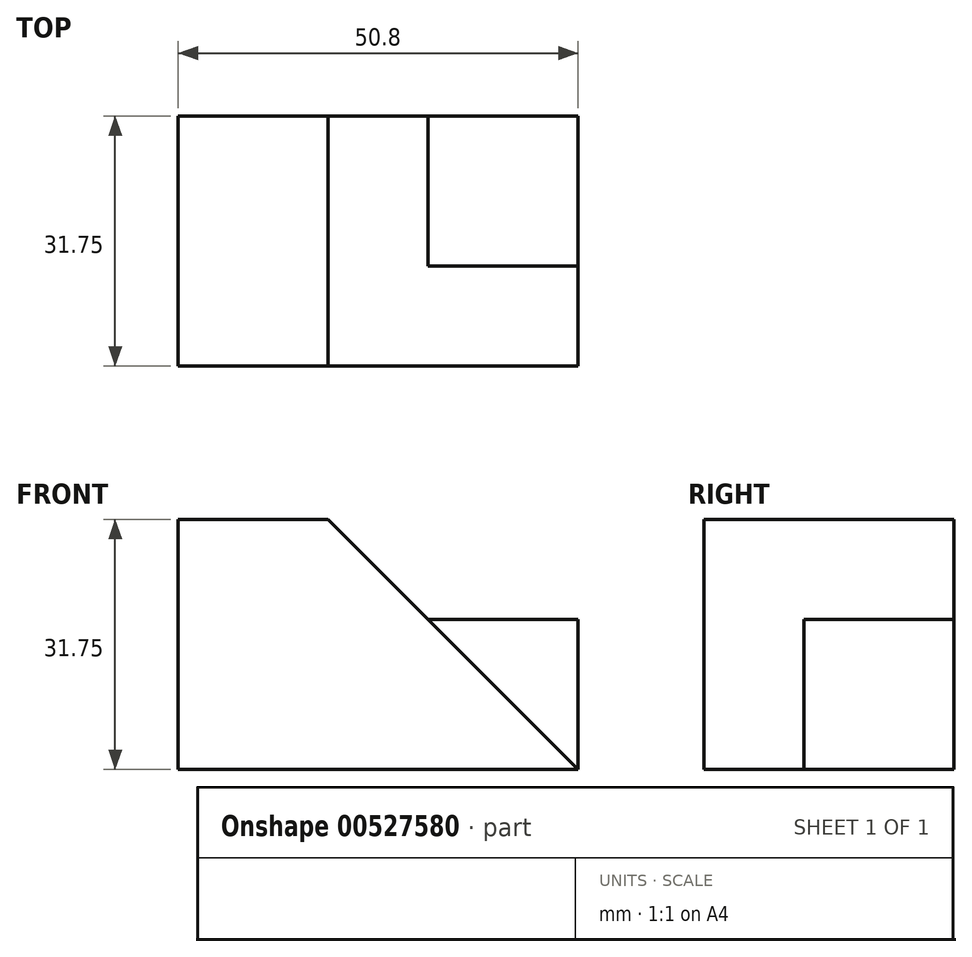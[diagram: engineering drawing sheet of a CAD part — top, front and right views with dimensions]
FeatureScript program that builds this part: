
annotation { "Feature Type Name" : "Feature", "Feature Type Description" : "" }
export const myFeature = defineFeature(function(context is Context, id is Id, definition is map)
    precondition{}
    {
        {
            var Q0;
            Q0=qCreatedBy(makeId("Front.planeOp"),FACE);
            var sketch = newSketch(context, id + "F0", { "sketchPlane" : qUnion([Q0])});
            skLineSegment(sketch, "E0", {"start": v(0, 0) * mm, "end": v(50.8, 0) * mm});
            skLineSegment(sketch, "E1", {"start": v(50.8, 0) * mm, "end": v(50.8, 31.75) * mm});
            skLineSegment(sketch, "E2", {"start": v(50.8, 31.75) * mm, "end": v(0, 31.75) * mm});
            skLineSegment(sketch, "E3", {"start": v(0, 31.75) * mm, "end": v(0, 0) * mm});
            skSolve(sketch);
        }
        {
            var Q0;
            Q0=makeQuery(id+"F0.imprint","IMPRINT",FACE,{"disambiguationData":[TD([[makeQuery(id+"F0.imprint","IMPRINT",EDGE,{"derivedFrom":sQuery(id+"F0.wireOp",EDGE,"E0")}),1.0]])]});
            extrude(context, id + "F1", {"entities" : qUnion([Q0]), "depth" : 31.75 * mm, "offsetDistance" : 25.4 * mm});
        }
        {
            var Q0;
            Q0=makeQuery(id+"F1.opExtrude","CAP_FACE",FACE,{"disambiguationData":[OSD([sQuery(id+"F0.wireOp",EDGE,"E0"),sQuery(id+"F0.wireOp",EDGE,"E1"),sQuery(id+"F0.wireOp",EDGE,"E2"),sQuery(id+"F0.wireOp",EDGE,"E3")])],"isStart":false});
            var sketch = newSketch(context, id + "F2", { "sketchPlane" : qUnion([Q0])});
            skLineSegment(sketch, "E4", {"start": v(0, 31.75) * mm, "end": v(19.05, 31.75) * mm});
            skLineSegment(sketch, "E5", {"start": v(19.05, 31.75) * mm, "end": v(50.8, 0) * mm});
            skSolve(sketch);
        }
        {
            var Q0;
            {var subQ0=sQuery(id+"F2.wireOp",EDGE,"E5");Q0=makeQuery(id+"F2.imprint","IMPRINT",FACE,{"disambiguationData":[TD([[makeQuery(id+"F2.imprint","IMPRINT",EDGE,{"derivedFrom":subQ0}),1.0]])]});}
            extrude(context, id + "F3", {"entities" : qUnion([Q0]), "operationType" : NewBodyOperationType.REMOVE, "oppositeDirection" : true, "depth" : 31.75 * mm, "offsetDistance" : 25.4 * mm});
        }
        {
            var Q0;
            Q0=makeQuery(id+"F1.opExtrude","CAP_FACE",FACE,{"disambiguationData":[OSD([sQuery(id+"F0.wireOp",EDGE,"E0"),sQuery(id+"F0.wireOp",EDGE,"E1"),sQuery(id+"F0.wireOp",EDGE,"E2"),sQuery(id+"F0.wireOp",EDGE,"E3")])],"isStart":true});
            var sketch = newSketch(context, id + "F4", { "sketchPlane" : qUnion([Q0])});
            skLineSegment(sketch, "E6", {"start": v(-50.8, 0) * mm, "end": v(-50.8, 19.05) * mm});
            skLineSegment(sketch, "E7", {"start": v(-50.8, 19.05) * mm, "end": v(-31.75, 19.05) * mm});
            skSolve(sketch);
        }
        {
            var Q0;
            {var subQ0=sQuery(id+"F4.wireOp",EDGE,"E6");Q0=makeQuery(id+"F4.imprint","IMPRINT",FACE,{"disambiguationData":[TD([[makeQuery(id+"F4.imprint","IMPRINT",EDGE,{"derivedFrom":subQ0}),-1.0]])]});}
            extrude(context, id + "F5", {"entities" : qUnion([Q0]), "oppositeDirection" : true, "depth" : 19.05 * mm, "offsetDistance" : 25.4 * mm});
        }
    });
